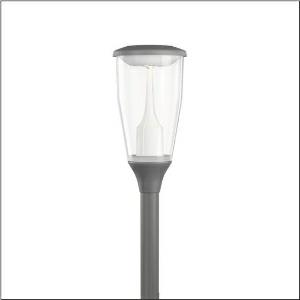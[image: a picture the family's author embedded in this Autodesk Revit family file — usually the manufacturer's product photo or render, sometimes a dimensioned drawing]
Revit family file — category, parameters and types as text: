
# Revit family: dl_11_iq___p1_0a_5xa5575bf14hp00022_48d3
name_source: partatom
category: Lighting Fixtures
units: mm (PartAtom-declared; Revit-internal decimal feet)

## family parameters
Cut with Voids When Loaded = No
Host = Face
Light Source = No
Part Type = Normal
Room Calculation Point = No
Round Connector Dimension = Use Diameter
Shared = No

## types (1)
- --- (1 x LED, 3950 lm, 33.6 W, 2200K)
    Apparent Load = 34 VA
    CIE Flux Codes = 33 63 91 94 100
    Color Rendering = 70
    Color Temperature = 2200K
    Default Elevation = 1800 mm
    Description = DL 11 iQ, mast luminaire, Module 540 iQ-SR, primary light control with 3 zone facetted reflector, of plastic, silver coated, highly specular, structured, primary optical cover: cover, of PMMA, transparent, light distribution: P1.0a, light emission: direct distribution, primary light characteristic: asymmetric, installation type: post-top, LED, High Power LED, light colour: 722, colour temperature: 2200K, control gear: iQ Street-Remote, control: Street-Remote, Auto-Match, Temp-Guard, Lumen-Switch, Night-Set, Smart-Wire, Light-Fading, Desk-Remote (wireless, voltage-free reading and setting of iQ features in the workshop via application-optimized NFC function/RFID function), optimised constant luminous flux control (CLO 2.0), mains connection: 220..240V, AC, 50/60Hz, connection cable pre-assembled, cable length: 5,5m, wiring characteristics: H07RN-F, 5-core, 1.5mm², start of lifetime: 34W, end of service life: 36W, luminaire housing, upper part, of diecast aluminium, coated, Siteco® metallic grey (DB 702S), spigot size: 76mm (post-top), mounting height: 3..5m, post-top mast mounting element, of diecast aluminium, coated, Siteco® metallic grey (DB 702S), Module 540 iQ-SR, traffic white (RAL 9016), equipment: Power, protection rating (complete): IP66, insulation class (complete): insulation class II (safety insulation), certification: CE, ENEC, ENEC+, VDE, impact resistance: IK07, packaging unit: 1 piece

Light Distribution: P1.0a
    Height = 665 mm
    Lamp = 1 x LED
    Lamp Light Flux = 3950 lm
    Lamp Power = 33.6 W
    Lamp count = 1
    Length = 334 mm
    Luminous efficacy = 118 lm/W
    Manufacturer = Siteco
    ModVariant = No
    Model = 5XA5575BF14HP00022
    Number of Poles = 1
    OnlyDefault = Yes
    Power Factor = 1
    Product Name = DL 11 iQ | P1.0a
    Product group = mast luminaire | pylon top
    ProductGroupID = 6100
    Protection Class = Protection class II
    Protection Degree = IP 66
    RLX_Detail_Level = 1
    RLX_Emergency_Light_Flux = 0 lm
    RLX_Emergency_Type = 0
    RLX_Emergency_Type_DB = No
    RlxData = <blob elided: 104333 chars, md5=67368c44>
    Socket = socket
    Standby Power = 0 W
    System Light Flux = 3950 lm
    System Power = 34 W
    Type Comments = factory setting: luminous flux: 100 % | dim-lin: 254 | 695 mA
    Type Image = l_1258354.jpg
    URL = http://relux.com
    VarID = @adj_053291
    Voltage = 0 V
    Weight = 0.00 kg
    Width = 0 mm  [stored 0 ft]

note: [stored X ft] marks values corroborated as IEEE doubles in the binary element streams (Revit-internal decimal feet)

## geometry (parser evidence)
native form markers: Blend x4, Sweep x11
no freeform markers — native parametric forms only
